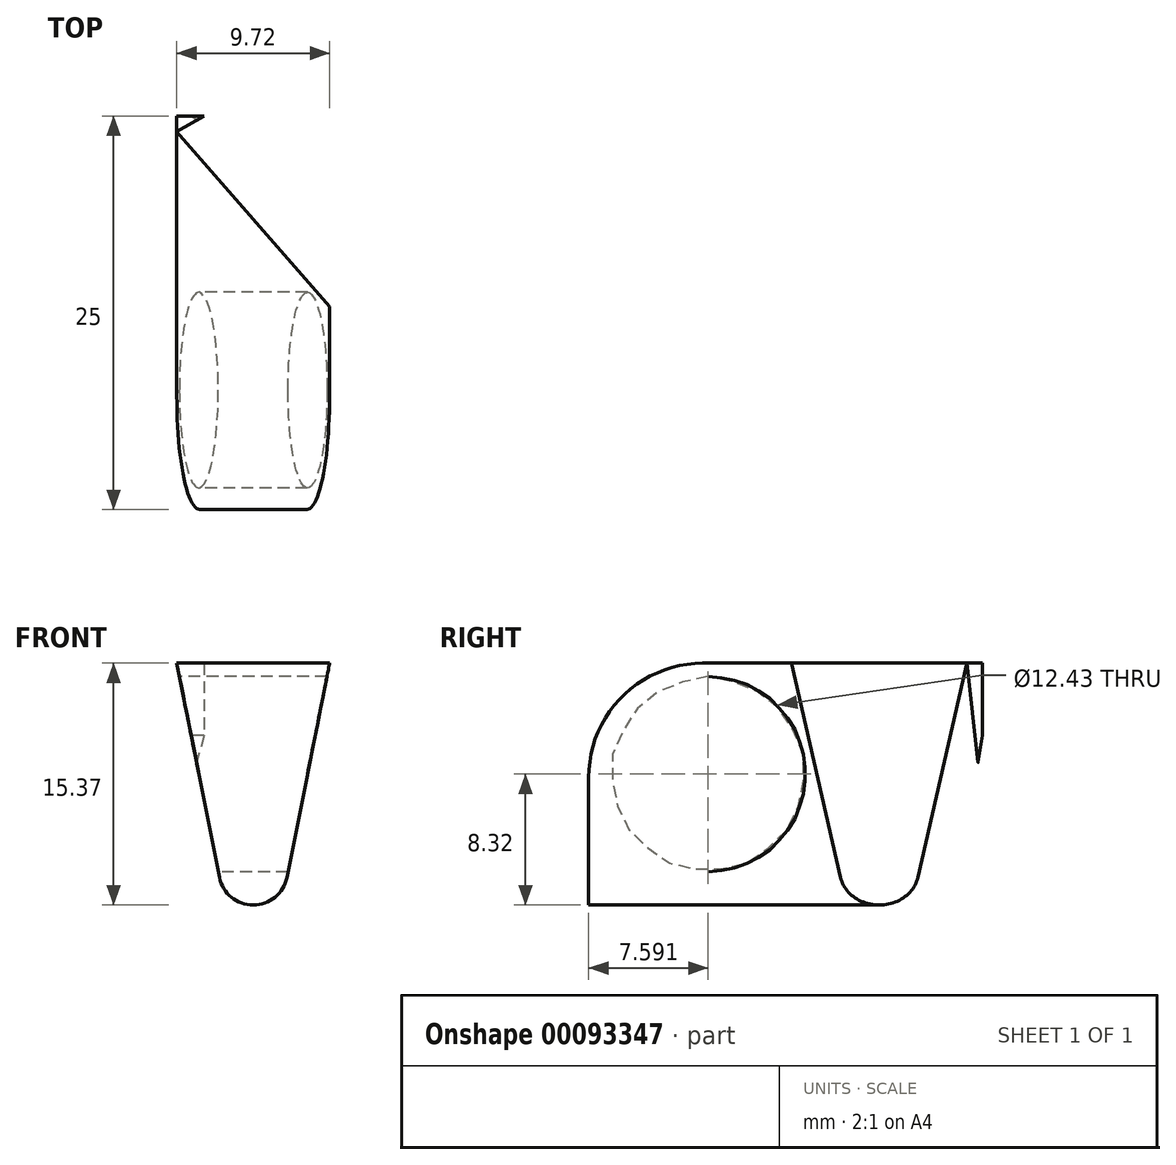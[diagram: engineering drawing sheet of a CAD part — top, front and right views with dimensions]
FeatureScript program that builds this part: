
annotation { "Feature Type Name" : "Feature", "Feature Type Description" : "" }
export const myFeature = defineFeature(function(context is Context, id is Id, definition is map)
    precondition{}
    {
        {
            var Q0;
            Q0=qCreatedBy(makeId("Front.planeOp"),FACE);
            var sketch = newSketch(context, id + "F0", { "sketchPlane" : qUnion([Q0])});
            skLineSegment(sketch, "E0", {"start": v(0, 7.5) * mm, "end": v(4.86, 7.5) * mm});
            skLineSegment(sketch, "E1", {"start": v(4.86, 7.5) * mm, "end": v(0, -16.87) * mm});
            skLineSegment(sketch, "E2.MirrorCS", {"start": v(0, 7.5) * mm, "end": v(-4.86, 7.5) * mm});
            skLineSegment(sketch, "E3.MirrorCS", {"start": v(-4.86, 7.5) * mm, "end": v(0, -16.87) * mm});
            skSolve(sketch);
        }
        {
            var Q0;
            Q0=makeQuery(id+"F0.imprint","IMPRINT",FACE,{"disambiguationData":[TD([[makeQuery(id+"F0.imprint","IMPRINT",EDGE,{"derivedFrom":sQuery(id+"F0.wireOp",EDGE,"E0")}),-1.0]])]});
            extrude(context, id + "F1", {"entities" : qUnion([Q0]), "depth" : 25 * mm});
        }
        {
            var Q0;
            Q0=makeQuery(id+"F1.opExtrude","SWEPT_EDGE",EDGE,{"disambiguationData":[OSD([sQuery(id+"F0.wireOp",EDGE,"E1"),sQuery(id+"F0.wireOp",EDGE,"E3.MirrorCS")])]});
            fillet(context, id + "F2", {"entities" : qUnion([Q0]), "radius" : 2.19 * mm, "tangentPropagation" : true, "allowEdgeOverflow" : false});
        }
        {
            var Q0;
            Q0=qCreatedBy(makeId("Right.planeOp"),FACE);
            var sketch = newSketch(context, id + "F3", { "sketchPlane" : qUnion([Q0])});
            skCircle(sketch, "E4", {"center": v(-42.66, 14.92) * mm, "radius": 44.56 * mm});
            skLineSegment(sketch, "E5", {"start": v(5.76, -21.28) * mm, "end": v(-16.68, -21.28) * mm});
            skCircle(sketch, "E6", {"center": v(-19.39, -2.27) * mm, "radius": 8.65 * mm});
            skLineSegment(sketch, "E7", {"start": v(1.53, 9.2) * mm, "end": v(1.53, -21.28) * mm});
            skSolve(sketch);
        }
        {
            var Q0;
            {var subQ3=sQuery(id+"F3.wireOp",EDGE,"E7");Q0=makeQuery(id+"F3.imprint","IMPRINT",FACE,{"disambiguationData":[TD([[makeQuery(id+"F3.imprint","IMPRINT",EDGE,{"derivedFrom":subQ3}),-1.0]])]});}
            extrude(context, id + "F4", {"entities" : qUnion([Q0]), "operationType" : NewBodyOperationType.REMOVE, "oppositeDirection" : true, "depth" : 25 * mm, "hasSecondDirection" : true, "secondDirectionOppositeDirection" : false, "secondDirectionDepth" : 25 * mm});
        }
        {
            var Q0;
            Q0=makeQuery(id+"F4.boolean.opBoolean","INTERSECT",EDGE,{"derivedFrom":[makeQuery(id+"F1.opExtrude","CAP_FACE",FACE,{"disambiguationData":[OSD([sQuery(id+"F0.wireOp",EDGE,"E0"),sQuery(id+"F0.wireOp",EDGE,"E1"),sQuery(id+"F0.wireOp",EDGE,"E2.MirrorCS"),sQuery(id+"F0.wireOp",EDGE,"E3.MirrorCS")])],"isStart":true}),makeQuery(id+"F4.opExtrude","SWEPT_FACE",FACE,{"disambiguationData":[OSD([sQuery(id+"F3.wireOp",EDGE,"E4")])]})]});
            chamfer(context, id + "F5", {"entities" : qUnion([Q0]), "width" : 5.5 * mm, "tangentPropagation" : true});
        }
        {
            var Q0;
            Q0=makeQuery(id+"F1.opExtrude","SWEPT_FACE",FACE,{"disambiguationData":[OSD([sQuery(id+"F0.wireOp",EDGE,"E0"),sQuery(id+"F0.wireOp",EDGE,"E2.MirrorCS")])]});
            var sketch = newSketch(context, id + "F6", { "sketchPlane" : qUnion([Q0])});
            skLineSegment(sketch, "E8", {"start": v(-4.86, -0.98) * mm, "end": v(7.9, -15.6) * mm});
            skLineSegment(sketch, "E9", {"start": v(7.9, -15.6) * mm, "end": v(7.9, 6.2) * mm});
            skLineSegment(sketch, "E10", {"start": v(7.9, 6.2) * mm, "end": v(-4.86, -0.98) * mm});
            skSolve(sketch);
        }
        {
            var Q0;
            Q0 = qSketchRegion(id + "F6", true);
            extrude(context, id + "F7", {"entities" : qUnion([Q0]), "operationType" : NewBodyOperationType.REMOVE, "oppositeDirection" : true, "depth" : 25 * mm});
        }
        {
            var Q0;
            Q0=qCreatedBy(makeId("Right.planeOp"),FACE);
            var sketch = newSketch(context, id + "F8", { "sketchPlane" : qUnion([Q0])});
            skCircle(sketch, "E11", {"center": v(-17.4, 0.45) * mm, "radius": 6.21 * mm});
            skSolve(sketch);
        }
        {
            var Q0;
            Q0=makeQuery(id+"F8.imprint","IMPRINT",FACE,{"disambiguationData":[TD([[makeQuery(id+"F8.imprint","IMPRINT",EDGE,{"derivedFrom":sQuery(id+"F8.wireOp",EDGE,"E11")}),1.0]])]});
            extrude(context, id + "F9", {"entities" : qUnion([Q0]), "operationType" : NewBodyOperationType.REMOVE, "depth" : 25 * mm, "hasSecondDirection" : true, "secondDirectionOppositeDirection" : true, "secondDirectionDepth" : 25 * mm});
        }
        {
            var Q0;
            Q0=makeQuery(id+"F1.opExtrude","CAP_EDGE",EDGE,{"disambiguationData":[OSD([sQuery(id+"F0.wireOp",EDGE,"E0"),sQuery(id+"F0.wireOp",EDGE,"E2.MirrorCS")])],"isStart":false});
            fillet(context, id + "F10", {"entities" : qUnion([Q0]), "radius" : 7.24 * mm, "tangentPropagation" : true, "allowEdgeOverflow" : false});
        }
    });
